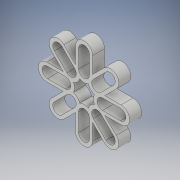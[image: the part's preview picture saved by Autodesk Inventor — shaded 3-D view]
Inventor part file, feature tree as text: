
AUTODESK INVENTOR PART (.ipt)
format: ipt  version: 2019 (Build 230136000, 136)  size: 246,272 bytes
history: native  units: mm
features: extrude x1, sketch x1
ambient origin geometry x8: Origin, YZ Plane, XZ Plane, XY Plane, X Axis, Y Axis, Z Axis, Center Point
bodies: Solid1 (feature_tree)
feature tree (2):
  extrude  "Extrusion1"  Depth=10.0mm
  sketch  "Sketch1"  dims[d1=80.0mm d2=4.0mm d3=15.0mm d4=360.0deg d6=0.5mm d7=0.5mm d8=0.5mm d9=0.5mm d10=0.5mm d11=0.5mm d12=0.5mm d13=0.5mm d14=18.0mm d15=80.0mm d17=360.0deg d19=10.0mm d20=0.0mm]
